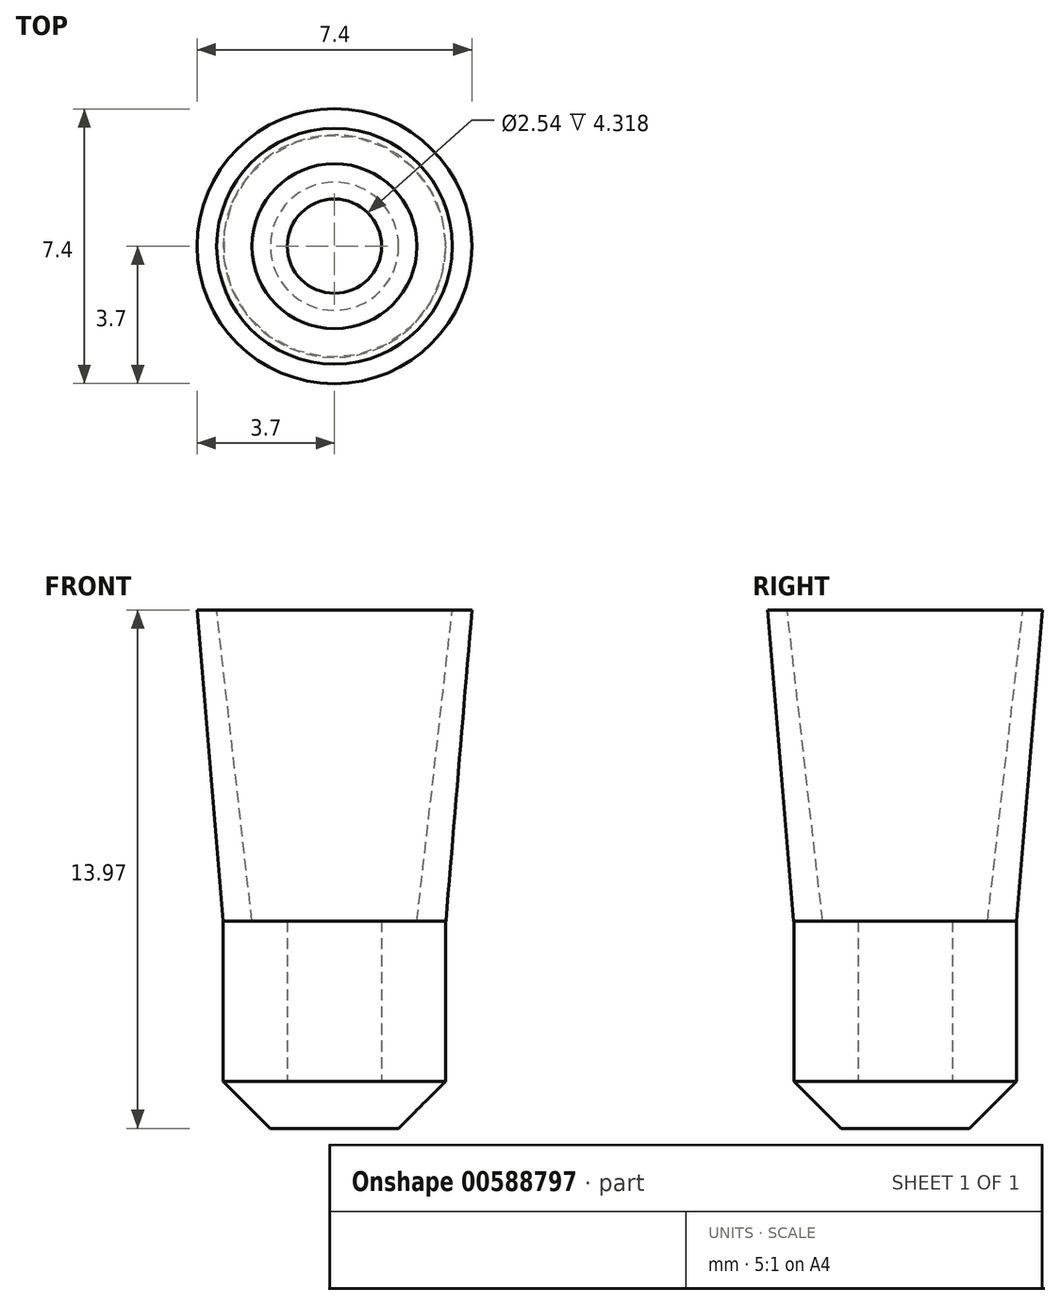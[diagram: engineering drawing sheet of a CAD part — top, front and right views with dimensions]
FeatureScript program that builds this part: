
annotation { "Feature Type Name" : "Feature", "Feature Type Description" : "" }
export const myFeature = defineFeature(function(context is Context, id is Id, definition is map)
    precondition{}
    {
        {
            var Q0;
            Q0=qCreatedBy(makeId("Top.planeOp"),FACE);
            var sketch = newSketch(context, id + "F0", { "sketchPlane" : qUnion([Q0])});
            skCircle(sketch, "E0", {"center": v(0, 0) * mm, "radius": 0.97 * mm});
            skCircle(sketch, "E1.0", {"center": v(0, 0) * mm, "radius": 3 * mm});
            skSolve(sketch);
        }
        {
            var Q0;
            Q0=makeQuery(id+"F0.imprint","IMPRINT",FACE,{"disambiguationData":[TD([[makeQuery(id+"F0.imprint","IMPRINT",EDGE,{"derivedFrom":sQuery(id+"F0.wireOp",EDGE,"E0")}),1.0]])]});
            var Q1;
            Q1=makeQuery(id+"F0.imprint","IMPRINT",FACE,{"disambiguationData":[TD([[makeQuery(id+"F0.imprint","IMPRINT",EDGE,{"derivedFrom":sQuery(id+"F0.wireOp",EDGE,"E0")}),-1.0]])]});
            extrude(context, id + "F1", {"entities" : qUnion([Q0, Q1]), "depth" : 1.27 * mm, "offsetDistance" : 25.4 * mm});
        }
        {
            var Q0;
            Q0=makeQuery(id+"F1.opExtrude","CAP_FACE",FACE,{"disambiguationData":[OSD([sQuery(id+"F0.wireOp",EDGE,"E1.0")])],"isStart":false});
            var sketch = newSketch(context, id + "F2", { "sketchPlane" : qUnion([Q0])});
            skCircle(sketch, "E2", {"center": v(0, 0) * mm, "radius": 1.27 * mm});
            skCircle(sketch, "E3.0", {"center": v(0, 0) * mm, "radius": 3.3 * mm});
            skSolve(sketch);
        }
        {
            var Q0;
            Q0=makeQuery(id+"F2.imprint","IMPRINT",FACE,{"disambiguationData":[TD([[makeQuery(id+"F2.imprint","IMPRINT",EDGE,{"derivedFrom":sQuery(id+"F2.wireOp",EDGE,"E2")}),-1.0]])]});
            extrude(context, id + "F3", {"entities" : qUnion([Q0]), "operationType" : NewBodyOperationType.ADD, "depth" : 4.32 * mm, "offsetDistance" : 25.4 * mm});
        }
        {
            var Q0;
            Q0=makeQuery(id+"F1.opExtrude","CAP_EDGE",EDGE,{"disambiguationData":[OSD([sQuery(id+"F0.wireOp",EDGE,"E1.0")])],"isStart":true});
            chamfer(context, id + "F4", {"entities" : qUnion([Q0]), "width" : 1.27 * mm, "tangentPropagation" : true});
        }
        {
            var Q0;
            Q0=makeQuery(id+"F3.opExtrude","CAP_FACE",FACE,{"disambiguationData":[OSD([sQuery(id+"F0.wireOp",EDGE,"E1.0"),sQuery(id+"F2.wireOp",EDGE,"E2")])],"isStart":false});
            var sketch = newSketch(context, id + "F5", { "sketchPlane" : qUnion([Q0])});
            skCircle(sketch, "E4", {"center": v(0, 0) * mm, "radius": 1.27 * mm});
            skSolve(sketch);
        }
        {
            var Q0;
            Q0=makeQuery(id+"F5.imprint","IMPRINT",FACE,{"disambiguationData":[TD([[makeQuery(id+"F5.imprint","IMPRINT",EDGE,{"derivedFrom":sQuery(id+"F5.wireOp",EDGE,"E4")}),-1.0]])]});
            cPlane(context, id + "F6", {"entities" : qUnion([Q0]), "cplaneType" : CPlaneType.OFFSET, "offset" : 8.38 * mm, "width" : 152.4 * mm, "height" : 152.4 * mm});
        }
        {
            var Q0;
            Q0=qCreatedBy(id+"F6.planeOp",FACE);
            var sketch = newSketch(context, id + "F7", { "sketchPlane" : qUnion([Q0])});
            skCircle(sketch, "E5.0", {"center": v(0, 0) * mm, "radius": 3.18 * mm});
            skSolve(sketch);
        }
        {
            var Q0;
            Q0=makeQuery(id+"F5.imprint","IMPRINT",FACE,{"disambiguationData":[TD([[makeQuery(id+"F5.imprint","IMPRINT",EDGE,{"derivedFrom":sQuery(id+"F5.wireOp",EDGE,"E4")}),-1.0]])]});
            cPlane(context, id + "F8", {"entities" : qUnion([Q0]), "cplaneType" : CPlaneType.OFFSET, "offset" : 0 * mm, "width" : 152.4 * mm, "height" : 152.4 * mm});
        }
        {
            var Q0;
            Q0=qCreatedBy(id+"F8.planeOp",FACE);
            var sketch = newSketch(context, id + "F9", { "sketchPlane" : qUnion([Q0])});
            skCircle(sketch, "E6", {"center": v(0, 0) * mm, "radius": 2.22 * mm});
            skSolve(sketch);
        }
        {
            var Q0;
            Q0=qCreatedBy(id+"F8.planeOp",FACE);
            var sketch = newSketch(context, id + "F10", { "sketchPlane" : qUnion([Q0])});
            skCircle(sketch, "E7", {"center": v(0, 0) * mm, "radius": 3 * mm});
            skSolve(sketch);
        }
        {
            var Q0;
            Q0=qCreatedBy(id+"F6.planeOp",FACE);
            var sketch = newSketch(context, id + "F11", { "sketchPlane" : qUnion([Q0])});
            skCircle(sketch, "E8", {"center": v(0, 0) * mm, "radius": 3.7 * mm});
            skSolve(sketch);
        }
        {
            var Q1;
            Q1=makeQuery(id+"F10.imprint","IMPRINT",FACE,{"disambiguationData":[TD([[makeQuery(id+"F10.imprint","IMPRINT",EDGE,{"derivedFrom":sQuery(id+"F10.wireOp",EDGE,"E7")}),1.0]])]});
            var Q2;
            Q2=makeQuery(id+"F11.imprint","IMPRINT",FACE,{"disambiguationData":[TD([[makeQuery(id+"F11.imprint","IMPRINT",EDGE,{"derivedFrom":sQuery(id+"F11.wireOp",EDGE,"E8")}),1.0]])]});
            loft(context, id + "F12", {"operationType" : NewBodyOperationType.ADD, "sheetProfilesArray" : [{ "sheetProfileEntities" : qUnion([Q1]) }, { "sheetProfileEntities" : qUnion([Q2]) }]});
        }
        {
            var Q1;
            Q1=makeQuery(id+"F9.imprint","IMPRINT",FACE,{"disambiguationData":[TD([[makeQuery(id+"F9.imprint","IMPRINT",EDGE,{"derivedFrom":sQuery(id+"F9.wireOp",EDGE,"E6")}),1.0]])]});
            var Q2;
            Q2=makeQuery(id+"F7.imprint","IMPRINT",FACE,{"disambiguationData":[TD([[makeQuery(id+"F7.imprint","IMPRINT",EDGE,{"derivedFrom":sQuery(id+"F7.wireOp",EDGE,"E5.0")}),1.0]])]});
            loft(context, id + "F13", {"operationType" : NewBodyOperationType.REMOVE, "sheetProfilesArray" : [{ "sheetProfileEntities" : qUnion([Q1]) }, { "sheetProfileEntities" : qUnion([Q2]) }]});
        }
    });
